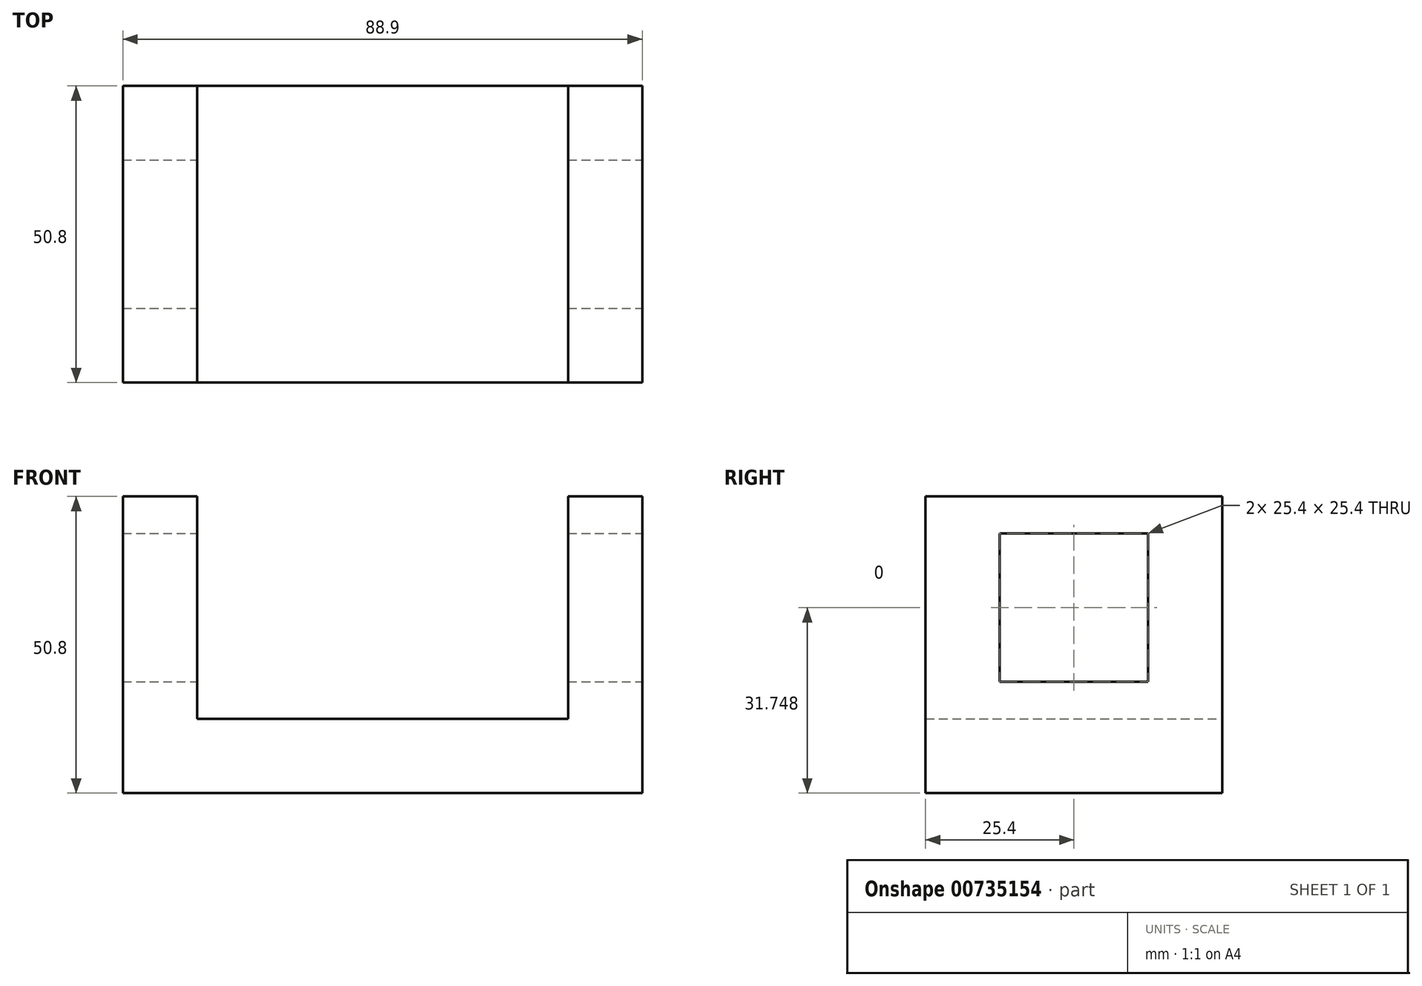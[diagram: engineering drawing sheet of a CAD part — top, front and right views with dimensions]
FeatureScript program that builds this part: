
annotation { "Feature Type Name" : "Feature", "Feature Type Description" : "" }
export const myFeature = defineFeature(function(context is Context, id is Id, definition is map)
    precondition{}
    {
        {
            var Q0;
            Q0=qCreatedBy(makeId("Front.planeOp"),FACE);
            var sketch = newSketch(context, id + "F0", { "sketchPlane" : qUnion([Q0])});
            skLineSegment(sketch, "E0", {"start": v(-57.48, 45.24) * mm, "end": v(-57.48, -5.56) * mm});
            skLineSegment(sketch, "E1", {"start": v(-57.48, -5.56) * mm, "end": v(31.42, -5.56) * mm});
            skLineSegment(sketch, "E2", {"start": v(31.42, -5.56) * mm, "end": v(31.42, 45.24) * mm});
            skLineSegment(sketch, "E3", {"start": v(31.42, 45.24) * mm, "end": v(18.72, 45.24) * mm});
            skLineSegment(sketch, "E4", {"start": v(-57.48, 45.24) * mm, "end": v(-44.78, 45.24) * mm});
            skLineSegment(sketch, "E5", {"start": v(-44.78, 45.24) * mm, "end": v(-44.78, 7.14) * mm});
            skLineSegment(sketch, "E6", {"start": v(18.72, 45.24) * mm, "end": v(18.72, 7.14) * mm});
            skLineSegment(sketch, "E7", {"start": v(-44.78, 7.14) * mm, "end": v(18.72, 7.14) * mm});
            skSolve(sketch);
        }
        {
            var Q0;
            Q0=makeQuery(id+"F0.imprint","IMPRINT",FACE,{"disambiguationData":[TD([[makeQuery(id+"F0.imprint","IMPRINT",EDGE,{"derivedFrom":sQuery(id+"F0.wireOp",EDGE,"E0")}),1.0]])]});
            extrude(context, id + "F1", {"entities" : qUnion([Q0]), "depth" : 50.8 * mm, "offsetDistance" : 25.4 * mm});
        }
        {
            var Q0;
            Q0=makeQuery(id+"F1.opExtrude","SWEPT_FACE",FACE,{"disambiguationData":[OSD([sQuery(id+"F0.wireOp",EDGE,"E2")])]});
            var sketch = newSketch(context, id + "F2", { "sketchPlane" : qUnion([Q0])});
            skLineSegment(sketch, "E8", {"start": v(-38.1, 38.89) * mm, "end": v(-38.1, 13.49) * mm});
            skLineSegment(sketch, "E9", {"start": v(-38.1, 13.49) * mm, "end": v(-12.7, 13.49) * mm});
            skLineSegment(sketch, "E10", {"start": v(-12.7, 13.49) * mm, "end": v(-12.7, 38.89) * mm});
            skLineSegment(sketch, "E11", {"start": v(-38.1, 38.89) * mm, "end": v(-12.7, 38.89) * mm});
            skSolve(sketch);
        }
        {
            var Q0;
            Q0=makeQuery(id+"F2.imprint","IMPRINT",FACE,{"disambiguationData":[TD([[makeQuery(id+"F2.imprint","IMPRINT",EDGE,{"derivedFrom":sQuery(id+"F2.wireOp",EDGE,"E8")}),1.0]])]});
            extrude(context, id + "F3", {"entities" : qUnion([Q0]), "operationType" : NewBodyOperationType.REMOVE, "endBound" : BoundingType.THROUGH_ALL, "oppositeDirection" : true, "depth" : 25.4 * mm, "offsetDistance" : 25.4 * mm});
        }
    });
